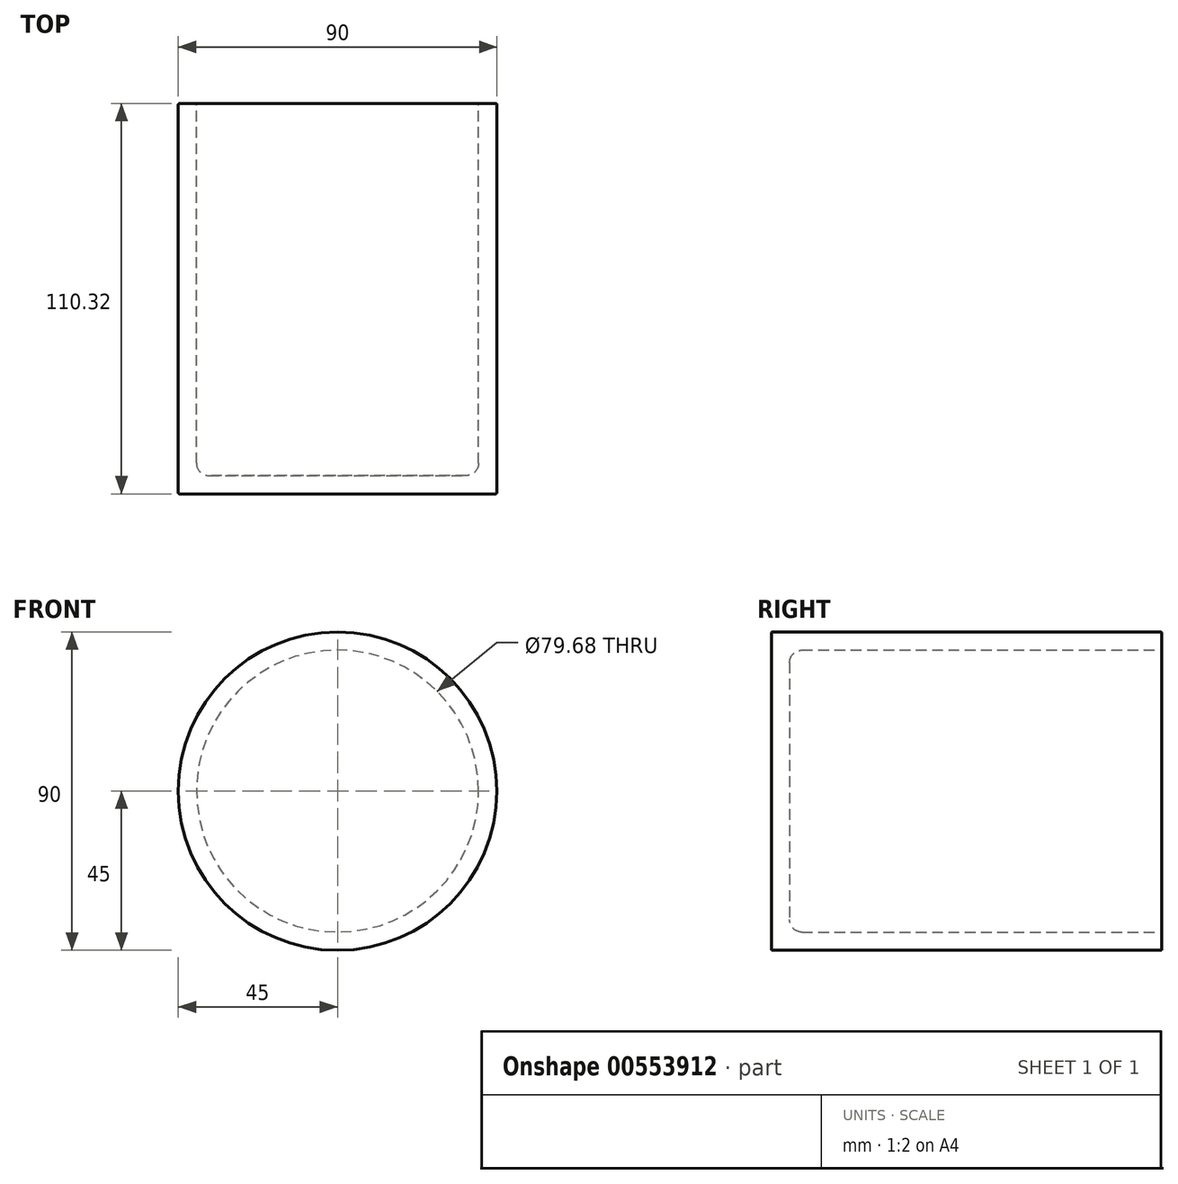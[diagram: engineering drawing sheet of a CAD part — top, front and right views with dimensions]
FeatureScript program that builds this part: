
annotation { "Feature Type Name" : "Feature", "Feature Type Description" : "" }
export const myFeature = defineFeature(function(context is Context, id is Id, definition is map)
    precondition{}
    {
        {
            var Q0;
            Q0=qCreatedBy(makeId("Top.planeOp"),FACE);
            var sketch = newSketch(context, id + "F0", { "sketchPlane" : qUnion([Q0])});
            skLineSegment(sketch, "E0", {"start": v(0, 34.84) * mm, "end": v(0, -85.16) * mm});
            skLineSegment(sketch, "E1", {"start": v(-70, -25.16) * mm, "end": v(70, -25.16) * mm});
            skLineSegment(sketch, "E2", {"start": v(-39.84, -16.5) * mm, "end": v(-39.84, 84.8) * mm});
            skLineSegment(sketch, "E3", {"start": v(-45, 84.8) * mm, "end": v(-45, -24.8) * mm});
            skLineSegment(sketch, "E4", {"start": v(-44.65, 85.16) * mm, "end": v(-40.2, 85.16) * mm});
            skArc(sketch, "E5", {"start": v(-44.65, 85.16) * mm, "mid": v(-44.9, 85.06) * mm, "end": v(-45, 84.8) * mm});
            skArc(sketch, "E6", {"start": v(-39.84, 84.8) * mm, "mid": v(-39.94, 85.06) * mm, "end": v(-40.2, 85.16) * mm});
            skLineSegment(sketch, "E7", {"start": v(-36.34, -20) * mm, "end": v(0, -20) * mm});
            skLineSegment(sketch, "E8", {"start": v(0, -20) * mm, "end": v(0, -25.16) * mm});
            skLineSegment(sketch, "E9", {"start": v(0, -25.16) * mm, "end": v(-44.65, -25.16) * mm});
            skArc(sketch, "E10", {"start": v(-39.84, -16.5) * mm, "mid": v(-38.82, -18.97) * mm, "end": v(-36.34, -20) * mm});
            skArc(sketch, "E11", {"start": v(-45, -24.8) * mm, "mid": v(-44.9, -25.06) * mm, "end": v(-44.65, -25.16) * mm});
            skSolve(sketch);
        }
        {
            var Q0;
            Q0=makeQuery(id+"F0.imprint","IMPRINT",FACE,{"disambiguationData":[TD([[makeQuery(id+"F0.imprint","IMPRINT",EDGE,{"derivedFrom":sQuery(id+"F0.wireOp",EDGE,"E2")}),1.0]])]});
            var Q1;
            Q1=sQuery(id+"F0.wireOp",EDGE,"E0");
            revolve(context, id + "F1", {"entities" : qUnion([Q0]), "axis" : qUnion([Q1]), "revolveType" : RevolveType.FULL});
        }
    });
